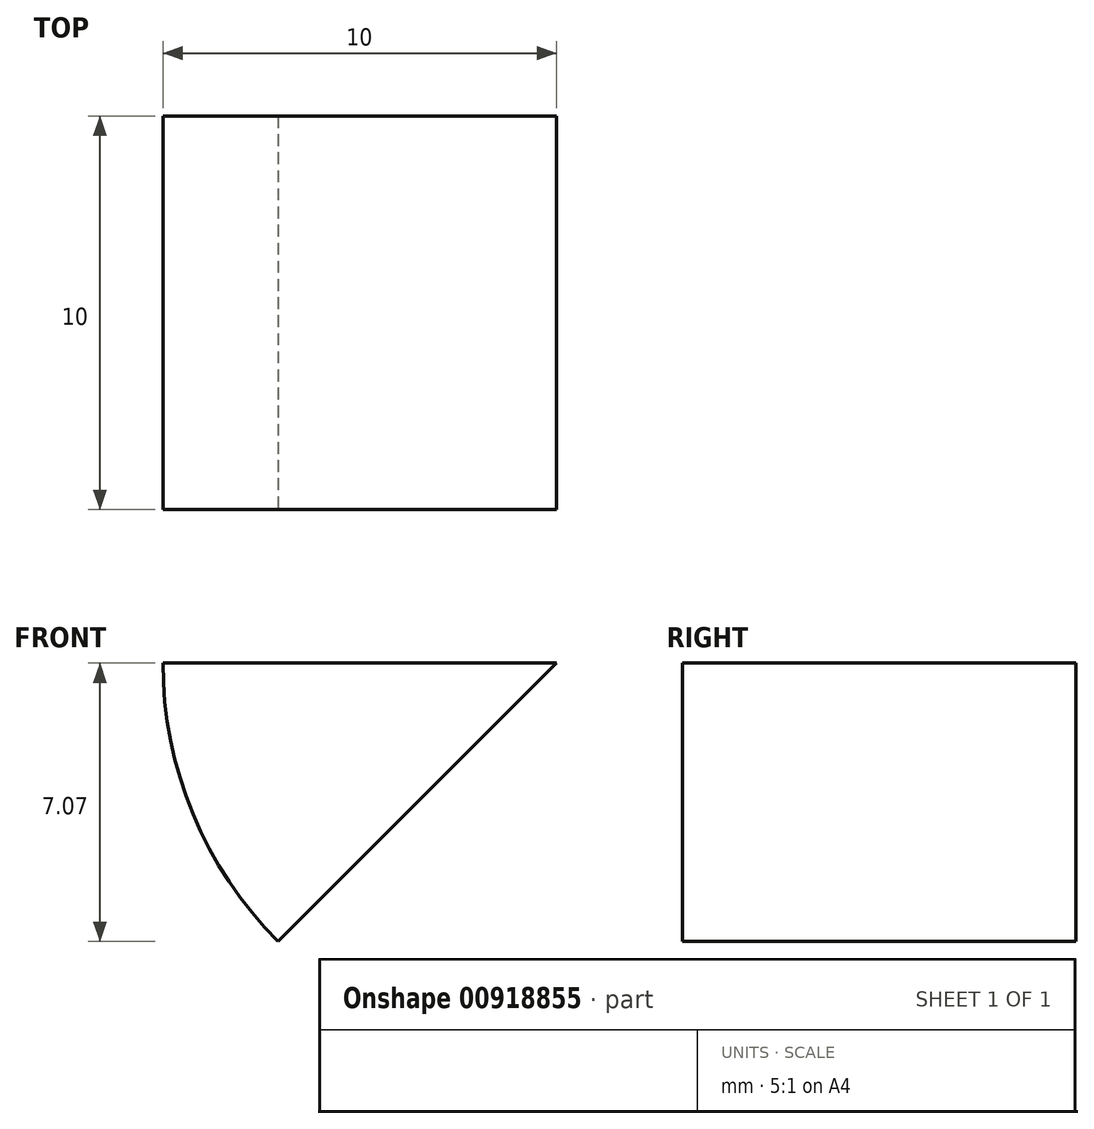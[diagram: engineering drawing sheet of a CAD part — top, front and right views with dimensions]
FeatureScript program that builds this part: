
annotation { "Feature Type Name" : "Feature", "Feature Type Description" : "" }
export const myFeature = defineFeature(function(context is Context, id is Id, definition is map)
    precondition{}
    {
        {
            var Q0;
            Q0=qCreatedBy(makeId("Top.planeOp"),FACE);
            var sketch = newSketch(context, id + "F0", { "sketchPlane" : qUnion([Q0])});
            skLineSegment(sketch, "E0.bottom", {"start": v(5, 5) * mm, "end": v(-5, 5) * mm});
            skLineSegment(sketch, "E0.top", {"start": v(5, -5) * mm, "end": v(-5, -5) * mm});
            skLineSegment(sketch, "E0.left", {"start": v(5, 5) * mm, "end": v(5, -5) * mm});
            skLineSegment(sketch, "E0.right", {"start": v(-5, 5) * mm, "end": v(-5, -5) * mm});
            skPoint(sketch, "E0.middle", {"position": v(0, 0) * mm});
            skSolve(sketch);
        }
        {
            var Q0;
            Q0=makeQuery(id+"F0.imprint","IMPRINT",FACE,{"disambiguationData":[TD([[makeQuery(id+"F0.imprint","IMPRINT",EDGE,{"derivedFrom":sQuery(id+"F0.wireOp",EDGE,"E0.bottom")}),1.0]])]});
            var Q1;
            Q1=sQuery(id+"F0.wireOp",EDGE,"E0.left");
            revolve(context, id + "F1", {"surfaceOperationType" : NewSurfaceOperationType.NEW, "entities" : qUnion([Q0]), "axis" : qUnion([Q1]), "revolveType" : RevolveType.ONE_DIRECTION, "angle" : 45 * degree});
        }
    });
